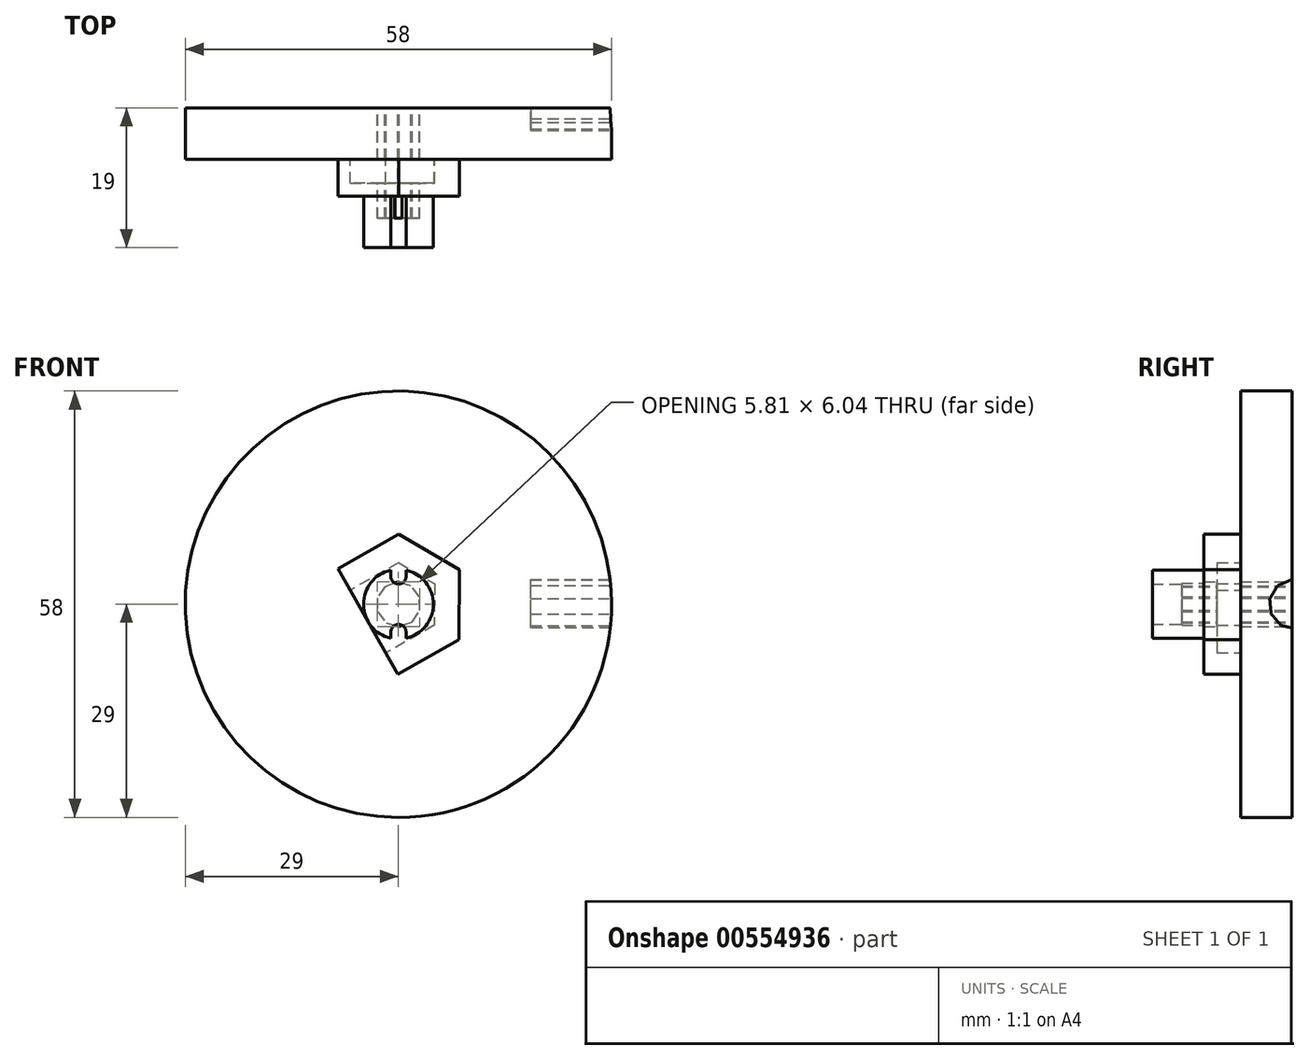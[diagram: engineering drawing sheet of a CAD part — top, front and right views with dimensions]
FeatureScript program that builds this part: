
annotation { "Feature Type Name" : "Feature", "Feature Type Description" : "" }
export const myFeature = defineFeature(function(context is Context, id is Id, definition is map)
    precondition{}
    {
        {
            var Q0;
            Q0=qCreatedBy(makeId("Front.planeOp"),FACE);
            var sketch = newSketch(context, id + "F0", { "sketchPlane" : qUnion([Q0])});
            skCircle(sketch, "E0", {"center": v(0, 0) * mm, "radius": 29 * mm});
            skSolve(sketch);
        }
        {
            var Q0;
            Q0=makeQuery(id+"F0.imprint","IMPRINT",FACE,{"disambiguationData":[TD([[makeQuery(id+"F0.imprint","IMPRINT",EDGE,{"derivedFrom":sQuery(id+"F0.wireOp",EDGE,"E0")}),1.0]])]});
            extrude(context, id + "F1", {"entities" : qUnion([Q0]), "depth" : 7 * mm, "offsetDistance" : 25 * mm});
        }
        {
            var Q0;
            Q0=makeQuery(id+"F1.opExtrude","CAP_FACE",FACE,{"disambiguationData":[OSD([sQuery(id+"F0.wireOp",EDGE,"E0")])],"isStart":false});
            var sketch = newSketch(context, id + "F2", { "sketchPlane" : qUnion([Q0])});
            skCircle(sketch, "E1", {"center": v(0, 0) * mm, "radius": 4.75 * mm});
            skCircle(sketch, "E2", {"center": v(0, 3.8) * mm, "radius": 1.05 * mm});
            skCircle(sketch, "E3", {"center": v(0, -3.8) * mm, "radius": 1.05 * mm});
            skLineSegment(sketch, "E4", {"start": v(0, 3.8) * mm, "end": v(0, -3.8) * mm});
            skLineSegment(sketch, "E5", {"start": v(-1.05, 3.8) * mm, "end": v(-1.05, 4.63) * mm});
            skLineSegment(sketch, "E6", {"start": v(1.05, 3.8) * mm, "end": v(1.05, 4.63) * mm});
            skLineSegment(sketch, "E7", {"start": v(-1.05, -3.8) * mm, "end": v(-1.05, -4.63) * mm});
            skLineSegment(sketch, "E8", {"start": v(1.05, -3.8) * mm, "end": v(1.05, -4.63) * mm});
            skSolve(sketch);
        }
        {
            var Q0;
            {var subQ4=sQuery(id+"F2.wireOp",EDGE,"E5");Q0=makeQuery(id+"F2.imprint","IMPRINT",FACE,{"disambiguationData":[TD([[makeQuery(id+"F2.imprint","IMPRINT",EDGE,{"derivedFrom":subQ4}),1.0]])]});}
            var Q1;
            {var subQ5=sQuery(id+"F2.wireOp",EDGE,"E6");Q1=makeQuery(id+"F2.imprint","IMPRINT",FACE,{"disambiguationData":[TD([[makeQuery(id+"F2.imprint","IMPRINT",EDGE,{"derivedFrom":subQ5}),-1.0]])]});}
            extrude(context, id + "F3", {"entities" : qUnion([Q0, Q1]), "operationType" : NewBodyOperationType.ADD, "depth" : 12 * mm, "offsetDistance" : 25 * mm});
        }
        {
            var Q0;
            Q0=qCreatedBy(makeId("Right.planeOp"),FACE);
            cPlane(context, id + "F4", {"entities" : qUnion([Q0]), "cplaneType" : CPlaneType.OFFSET, "offset" : 58 / 2 * mm, "width" : 150 * mm, "height" : 150 * mm});
        }
        {
            var Q0;
            Q0=qCreatedBy(id+"F4.planeOp",FACE);
            var sketch = newSketch(context, id + "F5", { "sketchPlane" : qUnion([Q0])});
            skCircle(sketch, "E9.cCircle", {"center": v(0.25, 0) * mm, "radius": 3.2 * mm, "construction": true});
            skLineSegment(sketch, "E9.0", {"start": v(-1.47, -2.9) * mm, "end": v(-2.84, -1.33) * mm});
            skLineSegment(sketch, "E9.1", {"start": v(-2.84, -1.33) * mm, "end": v(-3.03, 0.74) * mm});
            skLineSegment(sketch, "E9.2", {"start": v(-3.03, 0.74) * mm, "end": v(-1.97, 2.53) * mm});
            skLineSegment(sketch, "E9.3", {"start": v(-1.97, 2.53) * mm, "end": v(-0.06, 3.35) * mm});
            skLineSegment(sketch, "E9.4", {"start": v(-0.06, 3.35) * mm, "end": v(1.97, 2.9) * mm});
            skLineSegment(sketch, "E9.5", {"start": v(1.97, 2.9) * mm, "end": v(3.34, 1.33) * mm});
            skLineSegment(sketch, "E9.6", {"start": v(3.34, 1.33) * mm, "end": v(3.53, -0.74) * mm});
            skLineSegment(sketch, "E9.7", {"start": v(3.53, -0.74) * mm, "end": v(2.47, -2.53) * mm});
            skLineSegment(sketch, "E9.8", {"start": v(2.47, -2.53) * mm, "end": v(0.56, -3.35) * mm});
            skLineSegment(sketch, "E9.9", {"start": v(0.56, -3.35) * mm, "end": v(-1.47, -2.9) * mm});
            skPoint(sketch, "E9.0.midPoint", {"position": v(-2.15, -2.11) * mm});
            skSolve(sketch);
        }
        {
            var Q0;
            Q0=makeQuery(id+"F5.imprint","IMPRINT",FACE,{"disambiguationData":[TD([[makeQuery(id+"F5.imprint","IMPRINT",EDGE,{"derivedFrom":sQuery(id+"F5.wireOp",EDGE,"E9.0")}),-1.0]])]});
            extrude(context, id + "F6", {"entities" : qUnion([Q0]), "operationType" : NewBodyOperationType.REMOVE, "oppositeDirection" : true, "depth" : 11 * mm, "offsetDistance" : 25 * mm});
        }
        {
            var Q0;
            Q0=makeQuery(id+"F1.opExtrude","CAP_FACE",FACE,{"disambiguationData":[OSD([sQuery(id+"F0.wireOp",EDGE,"E0")])],"isStart":true});
            var sketch = newSketch(context, id + "F7", { "sketchPlane" : qUnion([Q0])});
            skCircle(sketch, "E10.cCircle", {"center": v(0, 0) * mm, "radius": 7 * mm, "construction": true});
            skLineSegment(sketch, "E10.0", {"start": v(0, -8.08) * mm, "end": v(-7, -4.04) * mm});
            skLineSegment(sketch, "E10.1", {"start": v(-7, -4.04) * mm, "end": v(-7, 4.04) * mm});
            skLineSegment(sketch, "E10.2", {"start": v(-7, 4.04) * mm, "end": v(0, 8.08) * mm});
            skLineSegment(sketch, "E10.3", {"start": v(0, 8.08) * mm, "end": v(7, 4.04) * mm});
            skLineSegment(sketch, "E10.4", {"start": v(7, 4.04) * mm, "end": v(7, -4.04) * mm});
            skLineSegment(sketch, "E10.5", {"start": v(7, -4.04) * mm, "end": v(0, -8.08) * mm});
            skPoint(sketch, "E10.0.midPoint", {"position": v(-3.5, -6.06) * mm});
            skSolve(sketch);
        }
        {
            var Q0;
            Q0=makeQuery(id+"F1.opExtrude","CAP_FACE",FACE,{"disambiguationData":[OSD([sQuery(id+"F0.wireOp",EDGE,"E0")])],"isStart":false});
            var sketch = newSketch(context, id + "F8", { "sketchPlane" : qUnion([Q0])});
            skCircle(sketch, "E11.cCircle", {"center": v(0, 0) * mm, "radius": 8.25 * mm, "construction": true});
            skLineSegment(sketch, "E11.0", {"start": v(0.07, 9.53) * mm, "end": v(8.29, 4.7) * mm});
            skLineSegment(sketch, "E11.1", {"start": v(8.29, 4.7) * mm, "end": v(8.21, -4.82) * mm});
            skLineSegment(sketch, "E11.2", {"start": v(8.21, -4.82) * mm, "end": v(-0.07, -9.53) * mm});
            skLineSegment(sketch, "E11.3", {"start": v(-0.07, -9.53) * mm, "end": v(-8.29, -4.7) * mm});
            skLineSegment(sketch, "E11.4", {"start": v(-8.29, -4.7) * mm, "end": v(-8.21, 4.82) * mm});
            skLineSegment(sketch, "E11.5", {"start": v(-8.21, 4.82) * mm, "end": v(0.07, 9.53) * mm});
            skPoint(sketch, "E11.0.midPoint", {"position": v(4.18, 7.11) * mm});
            skLineSegment(sketch, "E12", {"start": v(-8.21, 4.82) * mm, "end": v(-0.07, -9.53) * mm});
            skSolve(sketch);
        }
        {
            var Q0;
            Q0=makeQuery(id+"F8.imprint","IMPRINT",FACE,{"disambiguationData":[TD([[makeQuery(id+"F8.imprint","IMPRINT",EDGE,{"derivedFrom":makeQuery(id+"F3.opExtrude","CAP_EDGE",EDGE,{"disambiguationData":[OSD([sQuery(id+"F2.wireOp",EDGE,"E2")])],"isStart":true})}),-1.0]])]});
            var Q1;
            Q1=makeQuery(id+"F8.imprint","IMPRINT",FACE,{"disambiguationData":[TD([[makeQuery(id+"F8.imprint","IMPRINT",EDGE,{"derivedFrom":sQuery(id+"F8.wireOp",EDGE,"E11.0")}),-1.0]])]});
            extrude(context, id + "F9", {"entities" : qUnion([Q0, Q1]), "operationType" : NewBodyOperationType.ADD, "depth" : 5 * mm, "offsetDistance" : 25 * mm});
        }
        {
            var Q0;
            Q0=makeQuery(id+"F1.opExtrude","CAP_FACE",FACE,{"disambiguationData":[OSD([sQuery(id+"F0.wireOp",EDGE,"E0")])],"isStart":false});
            var sketch = newSketch(context, id + "F10", { "sketchPlane" : qUnion([Q0])});
            skCircle(sketch, "E13.cCircle", {"center": v(0, 0) * mm, "radius": 4.9 * mm, "construction": true});
            skLineSegment(sketch, "E13.0", {"start": v(0.04, 5.66) * mm, "end": v(4.92, 2.8) * mm});
            skLineSegment(sketch, "E13.1", {"start": v(4.92, 2.8) * mm, "end": v(4.88, -2.87) * mm});
            skLineSegment(sketch, "E13.2", {"start": v(4.88, -2.87) * mm, "end": v(-0.04, -5.66) * mm});
            skLineSegment(sketch, "E13.3", {"start": v(-0.04, -5.66) * mm, "end": v(-4.92, -2.8) * mm});
            skLineSegment(sketch, "E13.4", {"start": v(-4.92, -2.8) * mm, "end": v(-4.88, 2.87) * mm});
            skLineSegment(sketch, "E13.5", {"start": v(-4.88, 2.87) * mm, "end": v(0.04, 5.66) * mm});
            skPoint(sketch, "E13.0.midPoint", {"position": v(2.48, 4.23) * mm});
            skLineSegment(sketch, "E14", {"start": v(-4.88, 2.87) * mm, "end": v(-9.93, 0) * mm});
            skLineSegment(sketch, "E15", {"start": v(-0.04, -5.66) * mm, "end": v(-5.1, -8.52) * mm});
            skLineSegment(sketch, "E16", {"start": v(-9.93, 0) * mm, "end": v(-5.1, -8.52) * mm});
            skSolve(sketch);
        }
        {
            var Q0;
            Q0 = qSketchRegion(id + "F10", true);
            extrude(context, id + "F11", {"entities" : qUnion([Q0]), "operationType" : NewBodyOperationType.REMOVE, "depth" : 3.2 * mm, "offsetDistance" : 25 * mm});
        }
        {
            var Q0;
            Q0=makeQuery(id+"F1.opExtrude","CAP_FACE",FACE,{"disambiguationData":[OSD([sQuery(id+"F0.wireOp",EDGE,"E0")])],"isStart":true});
            var sketch = newSketch(context, id + "F12", { "sketchPlane" : qUnion([Q0])});
            skCircle(sketch, "E17.cCircle", {"center": v(0, 0) * mm, "radius": 2.88 * mm, "construction": true});
            skLineSegment(sketch, "E17.0", {"start": v(1.86, 2.38) * mm, "end": v(2.9, 0.83) * mm});
            skLineSegment(sketch, "E17.1", {"start": v(2.9, 0.83) * mm, "end": v(2.84, -1.03) * mm});
            skLineSegment(sketch, "E17.2", {"start": v(2.84, -1.03) * mm, "end": v(1.7, -2.5) * mm});
            skLineSegment(sketch, "E17.3", {"start": v(1.7, -2.5) * mm, "end": v(-0.1, -3.02) * mm});
            skLineSegment(sketch, "E17.4", {"start": v(-0.1, -3.02) * mm, "end": v(-1.86, -2.38) * mm});
            skLineSegment(sketch, "E17.5", {"start": v(-1.86, -2.38) * mm, "end": v(-2.9, -0.83) * mm});
            skLineSegment(sketch, "E17.6", {"start": v(-2.9, -0.83) * mm, "end": v(-2.84, 1.03) * mm});
            skLineSegment(sketch, "E17.7", {"start": v(-2.84, 1.03) * mm, "end": v(-1.7, 2.5) * mm});
            skLineSegment(sketch, "E17.8", {"start": v(-1.7, 2.5) * mm, "end": v(0.1, 3.02) * mm});
            skLineSegment(sketch, "E17.9", {"start": v(0.1, 3.02) * mm, "end": v(1.86, 2.38) * mm});
            skPoint(sketch, "E17.0.midPoint", {"position": v(2.38, 1.6) * mm});
            skSolve(sketch);
        }
        {
            var Q0;
            Q0=makeQuery(id+"F12.imprint","IMPRINT",FACE,{"disambiguationData":[TD([[makeQuery(id+"F12.imprint","IMPRINT",EDGE,{"derivedFrom":sQuery(id+"F12.wireOp",EDGE,"E17.0")}),-1.0]])]});
            extrude(context, id + "F13", {"entities" : qUnion([Q0]), "operationType" : NewBodyOperationType.REMOVE, "oppositeDirection" : true, "depth" : 15 * mm, "offsetDistance" : 25 * mm});
        }
    });
